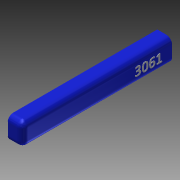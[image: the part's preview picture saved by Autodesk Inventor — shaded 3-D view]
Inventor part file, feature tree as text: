
AUTODESK INVENTOR PART (.ipt)
format: ipt  version: 2013 (Build 170138000, 138)  size: 346,624 bytes
history: native  units: in
note: dims shown in document units (in); Inventor stores cm internally (conversion verified against a paired STEP export)
features: reference x7, extrude x4, sketch x3, fillet x1, projected_geometry x1
ambient origin geometry x8: Origin, YZ Plane, XZ Plane, XY Plane, X Axis, Y Axis, Z Axis, Center Point
bodies: Solid1 (feature_tree)
feature tree (16):
  sketch  "Sketch1"  dims[d0=0.0625in d1=0.0in d3=1.0in]
  extrude  "Extrusion1"  Depth=1.0in
  extrude  "Extrusion2"  Depth=0.0625in
  extrude  "Extrusion3"  Depth=0.0625in TaperAngle=0.0deg
  fillet  "Fillet1"  Radius=1.3125in
  extrude  "Extrusion4"  Depth=6.0in
  reference  "Reference4"
  reference  "Reference5"
  sketch  "Sketch2"  dims[d7=1.0in d9=0.0625in]
  sketch  "Sketch3"  dims[d10=34.0in d11=0.0in d12=0.0625in d13=0.0in d14=1.3125in d15=6.0in d18=0.0625in d19=0.0in d20=0.0625in d21=0.0625in d23=2.5in d24=2.375in]
  reference  "Reference6"
  reference  "Reference7"
  reference  "Reference8"
  reference  "Reference9"
  reference  "Reference10"
  projected_geometry  "Projected Loop1"
